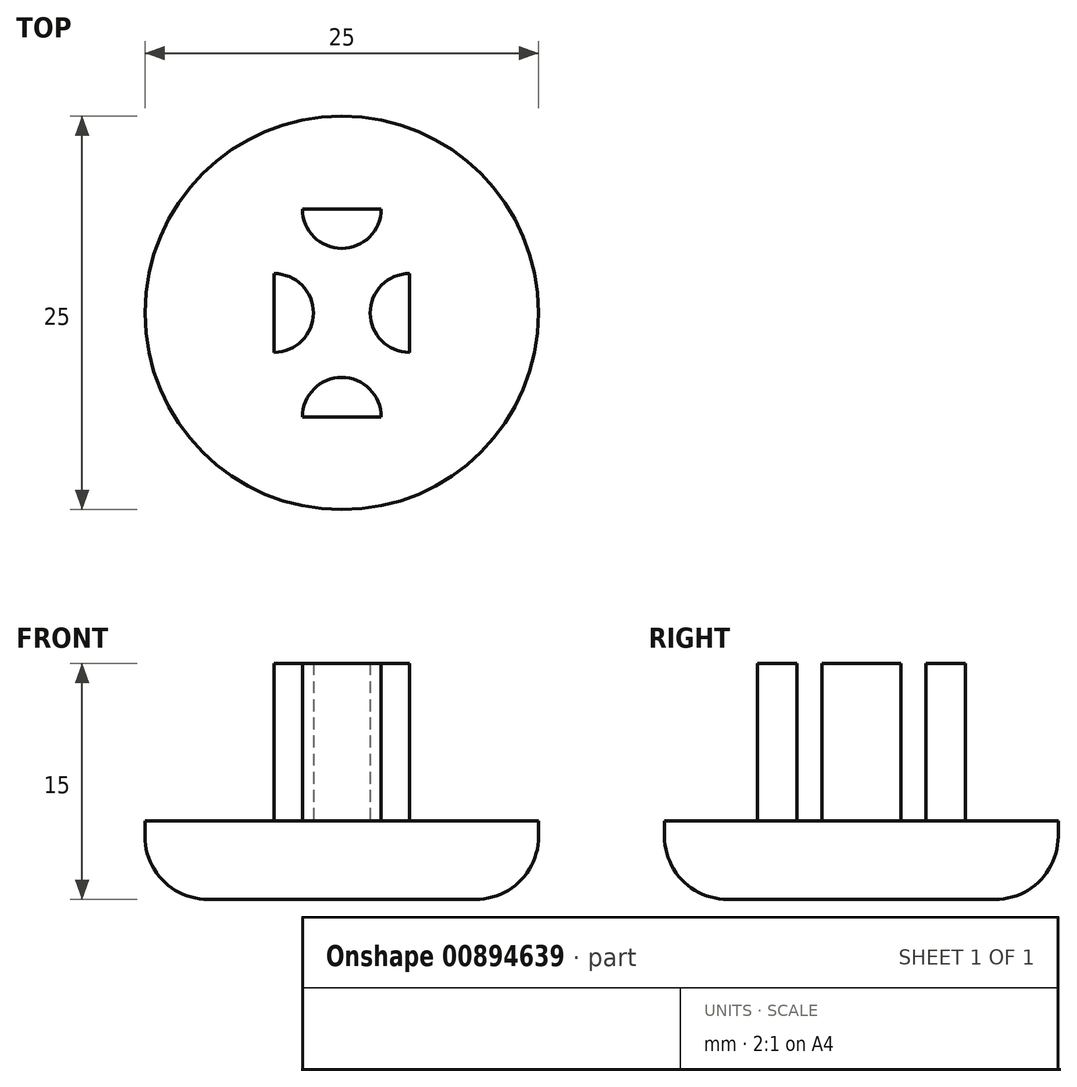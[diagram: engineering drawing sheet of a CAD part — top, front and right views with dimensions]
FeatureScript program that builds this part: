
annotation { "Feature Type Name" : "Feature", "Feature Type Description" : "" }
export const myFeature = defineFeature(function(context is Context, id is Id, definition is map)
    precondition{}
    {
        {
            var Q0;
            Q0=qCreatedBy(makeId("Top.planeOp"),FACE);
            var sketch = newSketch(context, id + "F0", { "sketchPlane" : qUnion([Q0])});
            skCircle(sketch, "E0", {"center": v(0, 0) * mm, "radius": 12.5 * mm});
            skSolve(sketch);
        }
        {
            var Q0;
            Q0 = qSketchRegion(id + "F0", true);
            extrude(context, id + "F1", {"entities" : qUnion([Q0]), "depth" : 5 * mm, "offsetDistance" : 25 * mm});
        }
        {
            var Q0;
            Q0=makeQuery(id+"F1.opExtrude","CAP_EDGE",EDGE,{"disambiguationData":[OSD([sQuery(id+"F0.wireOp",EDGE,"E0")])],"isStart":true});
            fillet(context, id + "F2", {"entities" : qUnion([Q0]), "radius" : 4 * mm, "tangentPropagation" : true, "allowEdgeOverflow" : false});
        }
        {
            var Q0;
            Q0=makeQuery(id+"F1.opExtrude","CAP_FACE",FACE,{"disambiguationData":[OSD([sQuery(id+"F0.wireOp",EDGE,"E0")])],"isStart":false});
            var sketch = newSketch(context, id + "F3", { "sketchPlane" : qUnion([Q0])});
            skLineSegment(sketch, "E1.bottom", {"start": v(4.3, 6.6) * mm, "end": v(-4.3, 6.6) * mm});
            skLineSegment(sketch, "E1.top", {"start": v(4.3, -6.6) * mm, "end": v(-4.3, -6.6) * mm});
            skLineSegment(sketch, "E1.left", {"start": v(4.3, 6.6) * mm, "end": v(4.3, -6.6) * mm});
            skLineSegment(sketch, "E1.right", {"start": v(-4.3, 6.6) * mm, "end": v(-4.3, -6.6) * mm});
            skPoint(sketch, "E1.middle", {"position": v(0, 0) * mm});
            skCircle(sketch, "E2", {"center": v(-4.3, 0) * mm, "radius": 2.5 * mm});
            skCircle(sketch, "E3", {"center": v(4.3, 0) * mm, "radius": 2.5 * mm});
            skCircle(sketch, "E4", {"center": v(0, 6.6) * mm, "radius": 2.5 * mm});
            skCircle(sketch, "E5", {"center": v(0, -6.6) * mm, "radius": 2.5 * mm});
            skSolve(sketch);
        }
        {
            var Q0;
            {var subQ0=sQuery(id+"F3.wireOp",EDGE,"E2");var subQ1=sQuery(id+"F3.wireOp",EDGE,"E1.right");var subQ2=makeQuery(id+"F3.imprint","INTERSECT",VERTEX,{"disambiguationData":[OD(0.0)],"derivedFrom":[subQ1,subQ0]});Q0=makeQuery(id+"F3.imprint","IMPRINT",FACE,{"disambiguationData":[TD([[makeQuery(id+"F3.imprint","IMPRINT",EDGE,{"disambiguationData":[TD([[subQ2,-1.0]])],"derivedFrom":subQ1}),1.0]])]});}
            var Q1;
            {var subQ0=sQuery(id+"F3.wireOp",EDGE,"E4");var subQ1=sQuery(id+"F3.wireOp",EDGE,"E1.bottom");var subQ2=makeQuery(id+"F3.imprint","INTERSECT",VERTEX,{"disambiguationData":[OD(0.0)],"derivedFrom":[subQ1,subQ0]});Q1=makeQuery(id+"F3.imprint","IMPRINT",FACE,{"disambiguationData":[TD([[makeQuery(id+"F3.imprint","IMPRINT",EDGE,{"disambiguationData":[TD([[subQ2,-1.0]])],"derivedFrom":subQ1}),1.0]])]});}
            var Q2;
            {var subQ0=sQuery(id+"F3.wireOp",EDGE,"E5");var subQ1=sQuery(id+"F3.wireOp",EDGE,"E1.top");var subQ2=makeQuery(id+"F3.imprint","INTERSECT",VERTEX,{"disambiguationData":[OD(0.0)],"derivedFrom":[subQ1,subQ0]});Q2=makeQuery(id+"F3.imprint","IMPRINT",FACE,{"disambiguationData":[TD([[makeQuery(id+"F3.imprint","IMPRINT",EDGE,{"disambiguationData":[TD([[subQ2,-1.0]])],"derivedFrom":subQ1}),-1.0]])]});}
            var Q3;
            {var subQ0=sQuery(id+"F3.wireOp",EDGE,"E3");var subQ1=sQuery(id+"F3.wireOp",EDGE,"E1.left");var subQ2=makeQuery(id+"F3.imprint","INTERSECT",VERTEX,{"disambiguationData":[OD(0.0)],"derivedFrom":[subQ1,subQ0]});Q3=makeQuery(id+"F3.imprint","IMPRINT",FACE,{"disambiguationData":[TD([[makeQuery(id+"F3.imprint","IMPRINT",EDGE,{"disambiguationData":[TD([[subQ2,-1.0]])],"derivedFrom":subQ1}),-1.0]])]});}
            extrude(context, id + "F4", {"entities" : qUnion([Q0, Q1, Q2, Q3]), "operationType" : NewBodyOperationType.ADD, "depth" : 10 * mm, "offsetDistance" : 25 * mm});
        }
    });
